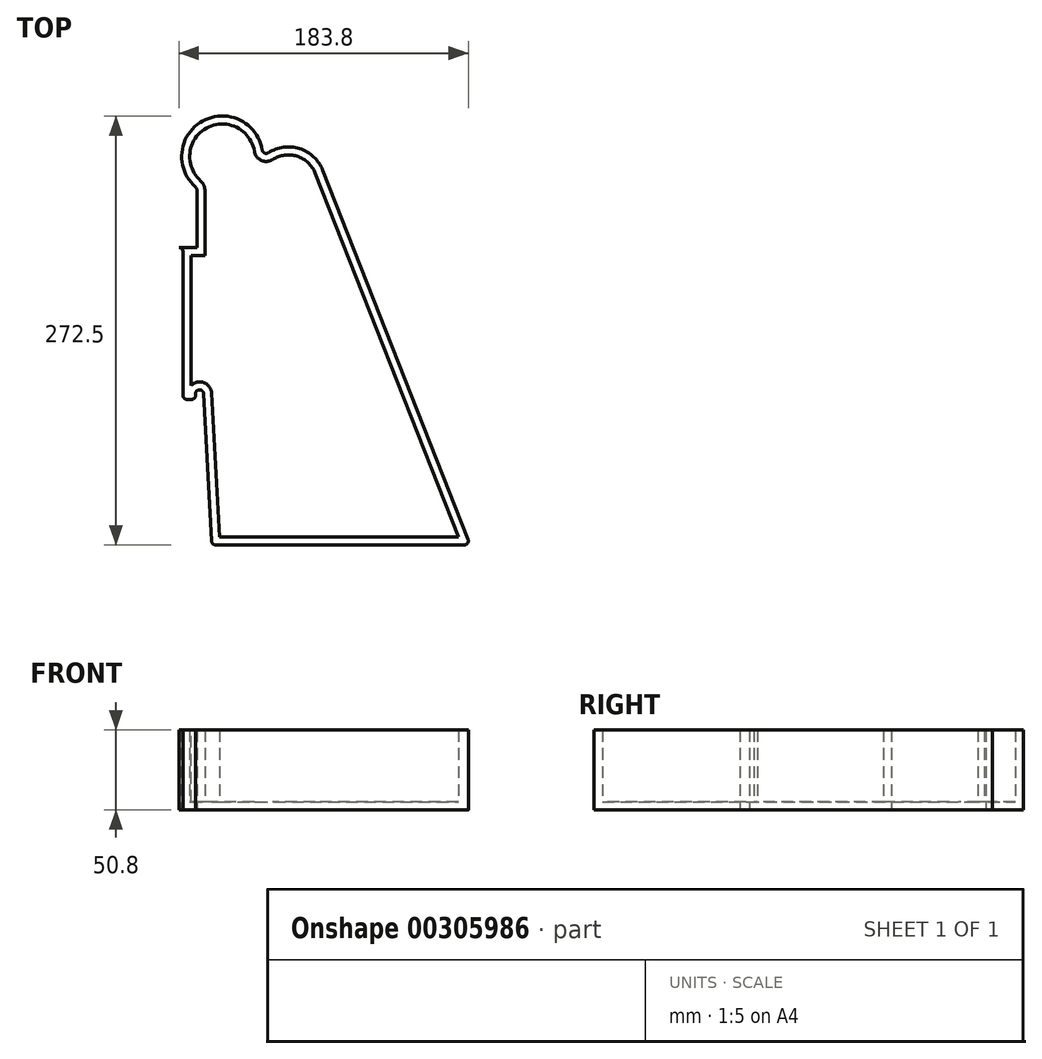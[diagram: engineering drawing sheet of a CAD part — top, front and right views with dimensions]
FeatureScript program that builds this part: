
annotation { "Feature Type Name" : "Feature", "Feature Type Description" : "" }
export const myFeature = defineFeature(function(context is Context, id is Id, definition is map)
    precondition{}
    {
        {
            var Q0;
            Q0=qCreatedBy(makeId("Top.planeOp"),FACE);
            var sketch = newSketch(context, id + "F0", { "sketchPlane" : qUnion([Q0])});
            skArc(sketch, "E0", {"start": v(-24.93, 61.95) * mm, "mid": v(-62.84, 80.38) * mm, "end": v(-67.32, 38.46) * mm});
            skArc(sketch, "E1", {"start": v(13.42, 49.15) * mm, "mid": v(-1.19, 62.85) * mm, "end": v(-21.04, 60.23) * mm});
            skLineSegment(sketch, "E2", {"start": v(-66.45, 36.55) * mm, "end": v(-66.45, 0) * mm});
            skLineSegment(sketch, "E3", {"start": v(-58.5, 0) * mm, "end": v(-55.95, 0) * mm});
            skLineSegment(sketch, "E4", {"start": v(-75.33, -2.54) * mm, "end": v(-75.33, -93.85) * mm});
            skLineSegment(sketch, "E5", {"start": v(-72.8, -96.4) * mm, "end": v(-69.81, -96.4) * mm});
            skLineSegment(sketch, "E6", {"start": v(-67.27, -93.85) * mm, "end": v(-67.27, -92.86) * mm});
            skLineSegment(sketch, "E7", {"start": v(-62.2, -92.72) * mm, "end": v(-57.06, -186.49) * mm});
            skLineSegment(sketch, "E8", {"start": v(-54.53, -188.9) * mm, "end": v(103.4, -188.9) * mm});
            skLineSegment(sketch, "E9", {"start": v(105.76, -185.42) * mm, "end": v(13.42, 49.15) * mm});
            skPoint(sketch, "E10.visualSharp", {"position": v(-66.45, -52.6) * mm});
            skPoint(sketch, "E11.visualSharp", {"position": v(-58.5, -52.6) * mm});
            skPoint(sketch, "E12.visualSharp", {"position": v(-75.33, -96.4) * mm});
            skArc(sketch, "E12.filletArc", {"start": v(-75.33, -93.85) * mm, "mid": v(-74.59, -95.65) * mm, "end": v(-72.8, -96.4) * mm});
            skPoint(sketch, "E13.visualSharp", {"position": v(-67.27, -96.4) * mm});
            skArc(sketch, "E13.filletArc", {"start": v(-69.81, -96.4) * mm, "mid": v(-68.02, -95.65) * mm, "end": v(-67.27, -93.85) * mm});
            skPoint(sketch, "E14.visualSharp", {"position": v(-67.27, 0) * mm});
            skArc(sketch, "E14.filletArc", {"start": v(-62.2, -92.72) * mm, "mid": v(-64.8, -90.32) * mm, "end": v(-67.27, -92.86) * mm});
            skPoint(sketch, "E15.visualSharp", {"position": v(-56.93, -188.9) * mm});
            skArc(sketch, "E15.filletArc", {"start": v(-57.06, -186.49) * mm, "mid": v(-56.27, -188.2) * mm, "end": v(-54.53, -188.9) * mm});
            skPoint(sketch, "E16.visualSharp", {"position": v(107.12, -188.9) * mm});
            skArc(sketch, "E16.filletArc", {"start": v(103.4, -188.9) * mm, "mid": v(105.5, -187.78) * mm, "end": v(105.76, -185.42) * mm});
            skPoint(sketch, "E17.visualSharp", {"position": v(-75.33, 0) * mm});
            skArc(sketch, "E17.filletArc", {"start": v(-75.33, -2.54) * mm, "mid": v(-76.08, -0.74) * mm, "end": v(-77.87, 0) * mm});
            skPoint(sketch, "E18.newPointA", {"position": v(-58.5, 14.75) * mm});
            skPoint(sketch, "E18.newPointB", {"position": v(-58.5, 0) * mm});
            skArc(sketch, "E18.filletArc", {"start": v(-55.95, 0) * mm, "mid": v(-57.75, -0.74) * mm, "end": v(-58.5, -2.54) * mm});
            skPoint(sketch, "E19.visualSharp", {"position": v(-24.6, 57.4) * mm});
            skArc(sketch, "E19.filletArc", {"start": v(-24.93, 61.95) * mm, "mid": v(-23.45, 60.04) * mm, "end": v(-21.04, 60.23) * mm});
            skPoint(sketch, "E20.visualSharp", {"position": v(-66.45, 37.74) * mm});
            skArc(sketch, "E20.filletArc", {"start": v(-66.45, 36.55) * mm, "mid": v(-66.68, 37.6) * mm, "end": v(-67.32, 38.46) * mm});
            skPoint(sketch, "E21.end.orphan", {"position": v(-43.46, 14.75) * mm});
            skLineSegment(sketch, "E22.trimOffspring", {"start": v(-77.87, 0) * mm, "end": v(-66.45, 0) * mm});
            skSolve(sketch);
        }
        {
            var Q0;
            Q0=makeQuery(id+"F0.imprint","IMPRINT",FACE,{"disambiguationData":[TD([[makeQuery(id+"F0.imprint","IMPRINT",EDGE,{"derivedFrom":sQuery(id+"F0.wireOp",EDGE,"E0")}),1.0]])]});
            extrude(context, id + "F1", {"entities" : qUnion([Q0]), "depth" : 50.8 * mm});
        }
        {
            var Q0;
            Q0=makeQuery(id+"F1.opExtrude","CAP_FACE",FACE,{"disambiguationData":[OSD([sQuery(id+"F0.wireOp",EDGE,"E0"),sQuery(id+"F0.wireOp",EDGE,"E1"),sQuery(id+"F0.wireOp",EDGE,"E2"),sQuery(id+"F0.wireOp",EDGE,"E4"),sQuery(id+"F0.wireOp",EDGE,"E5"),sQuery(id+"F0.wireOp",EDGE,"E6"),sQuery(id+"F0.wireOp",EDGE,"E7"),sQuery(id+"F0.wireOp",EDGE,"E8"),sQuery(id+"F0.wireOp",EDGE,"E9"),sQuery(id+"F0.wireOp",EDGE,"E12.filletArc"),sQuery(id+"F0.wireOp",EDGE,"E13.filletArc"),sQuery(id+"F0.wireOp",EDGE,"E14.filletArc"),sQuery(id+"F0.wireOp",EDGE,"E15.filletArc"),sQuery(id+"F0.wireOp",EDGE,"E16.filletArc"),sQuery(id+"F0.wireOp",EDGE,"E17.filletArc"),sQuery(id+"F0.wireOp",EDGE,"E19.filletArc"),sQuery(id+"F0.wireOp",EDGE,"E20.filletArc"),sQuery(id+"F0.wireOp",EDGE,"E22.trimOffspring")])],"isStart":false});
            shell(context, id + "F2", {"entities" : qUnion([Q0]), "thickness" : 5.08 * mm});
        }
    });
